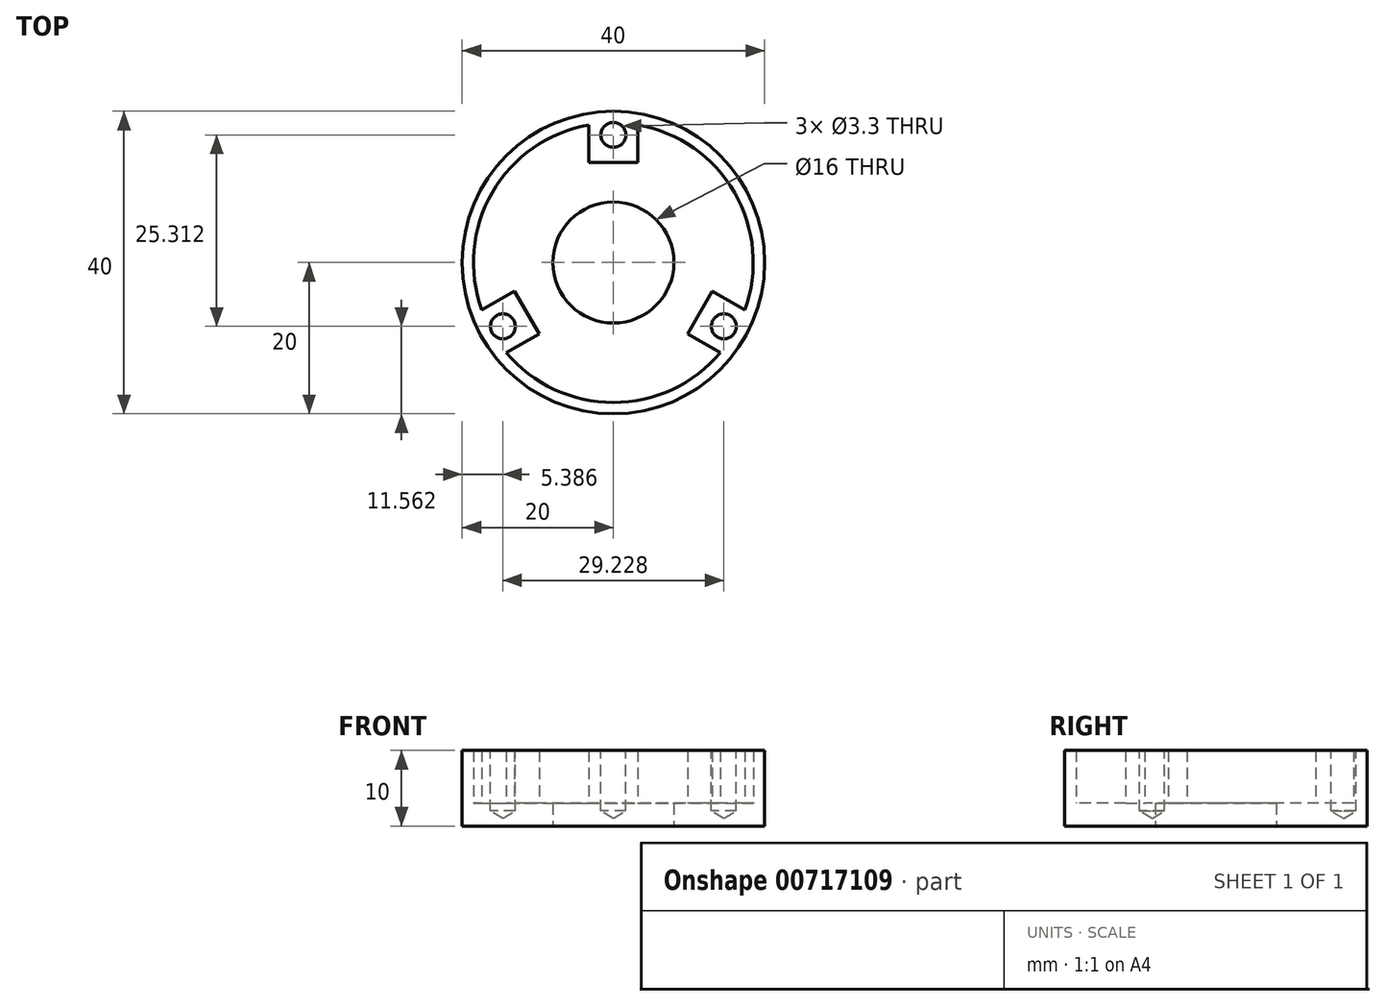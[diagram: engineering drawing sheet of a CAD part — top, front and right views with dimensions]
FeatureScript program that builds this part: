
annotation { "Feature Type Name" : "Feature", "Feature Type Description" : "" }
export const myFeature = defineFeature(function(context is Context, id is Id, definition is map)
    precondition{}
    {
        {
            var Q0;
            Q0=qCreatedBy(makeId("Front.planeOp"),FACE);
            var sketch = newSketch(context, id + "F0", { "sketchPlane" : qUnion([Q0])});
            skLineSegment(sketch, "E0", {"start": v(8, 0) * mm, "end": v(8, 3) * mm});
            skLineSegment(sketch, "E1", {"start": v(8, 3) * mm, "end": v(18.5, 3) * mm});
            skLineSegment(sketch, "E2", {"start": v(18.5, 3) * mm, "end": v(18.5, 10) * mm});
            skLineSegment(sketch, "E3", {"start": v(18.5, 10) * mm, "end": v(20, 10) * mm});
            skLineSegment(sketch, "E4", {"start": v(20, 10) * mm, "end": v(20, 0) * mm});
            skLineSegment(sketch, "E5", {"start": v(20, 0) * mm, "end": v(8, 0) * mm});
            skLineSegment(sketch, "E6", {"start": v(0, -58.88) * mm, "end": v(0, 98.37) * mm, "construction": true});
            skSolve(sketch);
        }
        {
            var Q0;
            Q0=makeQuery(id+"F0.imprint","IMPRINT",FACE,{"disambiguationData":[TD([[makeQuery(id+"F0.imprint","IMPRINT",EDGE,{"derivedFrom":sQuery(id+"F0.wireOp",EDGE,"E0")}),-1.0]])]});
            var Q1;
            Q1=sQuery(id+"F0.wireOp",EDGE,"E6");
            revolve(context, id + "F1", {"surfaceOperationType" : NewSurfaceOperationType.NEW, "entities" : qUnion([Q0]), "axis" : qUnion([Q1]), "revolveType" : RevolveType.FULL});
        }
        {
            var Q0;
            Q0=makeQuery(id+"F1.opRevolve","SWEPT_FACE",FACE,{"disambiguationData":[OSD([sQuery(id+"F0.wireOp",EDGE,"E1")])]});
            var sketch = newSketch(context, id + "F2", { "sketchPlane" : qUnion([Q0])});
            skLineSegment(sketch, "E7.top", {"start": v(-3.25, 13.21) * mm, "end": v(3.25, 13.21) * mm});
            skLineSegment(sketch, "E7.left", {"start": v(-3.25, 18.21) * mm, "end": v(-3.25, 13.21) * mm});
            skLineSegment(sketch, "E7.right", {"start": v(3.25, 18.21) * mm, "end": v(3.25, 13.21) * mm});
            skArc(sketch, "E8.0", {"start": v(3.25, 18.21) * mm, "mid": v(0, 18.5) * mm, "end": v(-3.25, 18.21) * mm});
            skSolve(sketch);
        }
        {
            var Q0;
            Q0 = qSketchRegion(id + "F2", true);
            var Q1;
            Q1=makeQuery(id+"F1.opRevolve","SWEPT_FACE",FACE,{"disambiguationData":[OSD([sQuery(id+"F0.wireOp",EDGE,"E3")])]});
            extrude(context, id + "F3", {"entities" : qUnion([Q0]), "endBound" : BoundingType.UP_TO_SURFACE, "depth" : 25 * mm, "endBoundEntityFace" : qUnion([Q1]), "offsetDistance" : 25 * mm});
        }
        {
            var Q0;
            Q0=makeQuery(id+"F3.opExtrude","SWEPT_BODY",BODY,{"disambiguationData":[OSD([sQuery(id+"F2.wireOp",EDGE,"E7.top"),sQuery(id+"F2.wireOp",EDGE,"E7.left"),sQuery(id+"F2.wireOp",EDGE,"E7.right"),sQuery(id+"F2.wireOp",EDGE,"E8.0")])]});
            var Q1;
            Q1=sQuery(id+"F0.wireOp",EDGE,"E6");
            circularPattern(context, id + "F4", {"operationType" : NewBodyOperationType.ADD, "entities" : qUnion([Q0]), "axis" : qUnion([Q1]), "angle" : 360 * degree, "instanceCount" : 3, "equalSpace" : true});
        }
        {
            var Q0;
            Q0=makeQuery(id+"F3.opExtrude","CAP_FACE",FACE,{"disambiguationData":[OSD([sQuery(id+"F2.wireOp",EDGE,"E7.top"),sQuery(id+"F2.wireOp",EDGE,"E7.left"),sQuery(id+"F2.wireOp",EDGE,"E7.right"),sQuery(id+"F2.wireOp",EDGE,"E8.0")])],"isStart":false});
            var sketch = newSketch(context, id + "F5", { "sketchPlane" : qUnion([Q0])});
            skPoint(sketch, "E9", {"position": v(0, 16.88) * mm});
            skPoint(sketch, "E10.1.0", {"position": v(-14.61, -8.44) * mm});
            skPoint(sketch, "E10.2.0", {"position": v(14.61, -8.44) * mm});
            skPoint(sketch, "E10.center", {"position": v(0, 0) * mm});
            skCircle(sketch, "E11", {"center": v(0, 0) * mm, "radius": 16.88 * mm, "construction": true});
            skSolve(sketch);
        }
        {
            var Q0;
            Q0=sQuery(id+"F5.wireOp",VERTEX,"E9");
            var Q1;
            Q1=sQuery(id+"F5.wireOp",VERTEX,"E10.2.0");
            var Q2;
            Q2=sQuery(id+"F5.wireOp",VERTEX,"E10.1.0");
            var Q3;
            Q3=makeQuery(id+"F1.opRevolve","SWEPT_BODY",BODY,{"disambiguationData":[OSD([sQuery(id+"F0.wireOp",EDGE,"E0"),sQuery(id+"F0.wireOp",EDGE,"E1"),sQuery(id+"F0.wireOp",EDGE,"E2"),sQuery(id+"F0.wireOp",EDGE,"E3"),sQuery(id+"F0.wireOp",EDGE,"E4"),sQuery(id+"F0.wireOp",EDGE,"E5")])]});
            var Q4;
            Q4=makeQuery(id+"F3.opExtrude","SWEPT_BODY",BODY,{"disambiguationData":[OSD([sQuery(id+"F2.wireOp",EDGE,"E7.top"),sQuery(id+"F2.wireOp",EDGE,"E7.left"),sQuery(id+"F2.wireOp",EDGE,"E7.right"),sQuery(id+"F2.wireOp",EDGE,"E8.0")])]});
            var Q5;
            Q5=makeQuery(id+"F4.opPattern","COPY",BODY,{"derivedFrom":makeQuery(id+"F3.opExtrude","SWEPT_BODY",BODY,{"disambiguationData":[OSD([sQuery(id+"F2.wireOp",EDGE,"E7.top"),sQuery(id+"F2.wireOp",EDGE,"E7.left"),sQuery(id+"F2.wireOp",EDGE,"E7.right"),sQuery(id+"F2.wireOp",EDGE,"E8.0")])]}),"instanceName":"2"});
            var Q6;
            Q6=makeQuery(id+"F4.opPattern","COPY",BODY,{"derivedFrom":makeQuery(id+"F3.opExtrude","SWEPT_BODY",BODY,{"disambiguationData":[OSD([sQuery(id+"F2.wireOp",EDGE,"E7.top"),sQuery(id+"F2.wireOp",EDGE,"E7.left"),sQuery(id+"F2.wireOp",EDGE,"E7.right"),sQuery(id+"F2.wireOp",EDGE,"E8.0")])]}),"instanceName":"1"});
            hole(context, id + "F6", {"style" : HoleStyle.SIMPLE, "endStyle" : HoleEndStyle.BLIND, "standardTappedOrClearance" : lookupTablePath({ "standard" : "ISO", "engagement" : "75%", "pitch" : "0.7 mm", "size" : "M4", "type" : "Tapped" }), "standardBlindInLast" : lookupTablePath({ "standard" : "ISO", "engagement" : "75%", "pitch" : "0.7 mm", "size" : "M4", "type" : "Tapped" }), "holeDiameter" : 3.3 * mm, "majorDiameter" : 4 * mm, "showTappedDepth" : true, "holeDepth" : 8 * mm, "isTappedThrough" : true, "tappedDepth" : 5.9 * mm, "tapClearance" : 3, "locations" : qUnion([Q0, Q1, Q2]), "scope" : qUnion([Q3, Q4, Q5, Q6])});
        }
    });
